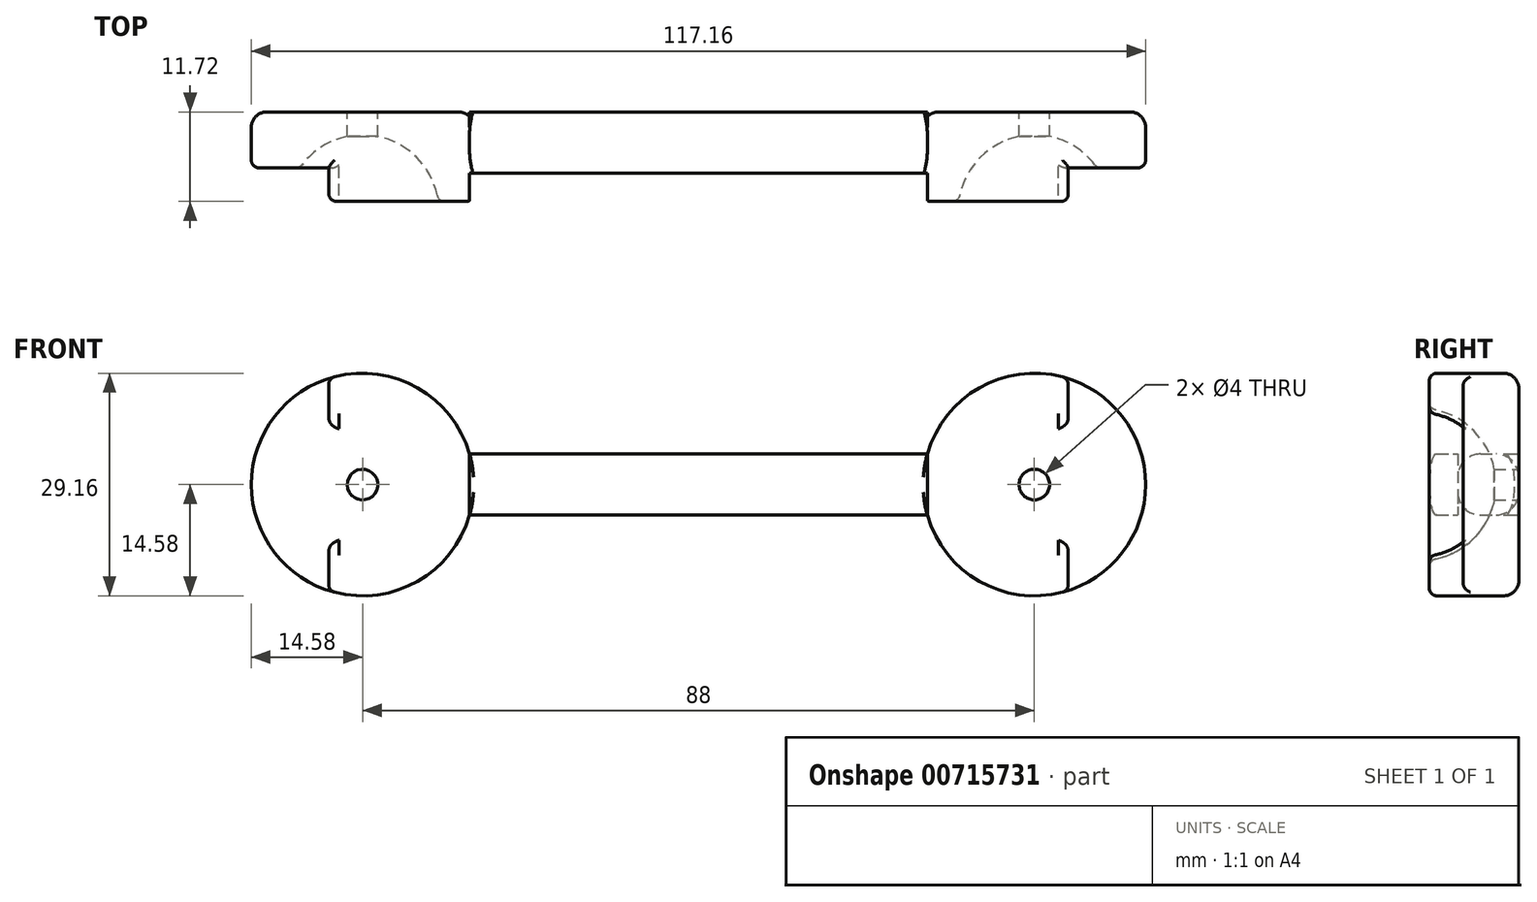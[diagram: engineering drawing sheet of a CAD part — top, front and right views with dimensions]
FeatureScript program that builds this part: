
annotation { "Feature Type Name" : "Feature", "Feature Type Description" : "" }
export const myFeature = defineFeature(function(context is Context, id is Id, definition is map)
    precondition{}
    {
        {
            var Q0;
            Q0=qCreatedBy(makeId("Front.planeOp"),FACE);
            var sketch = newSketch(context, id + "F0", { "sketchPlane" : qUnion([Q0])});
            skLineSegment(sketch, "E0.bottom", {"start": v(-30, 4) * mm, "end": v(30, 4) * mm});
            skLineSegment(sketch, "E0.top", {"start": v(-30, -4) * mm, "end": v(30, -4) * mm});
            skLineSegment(sketch, "E0.left", {"start": v(-30, 4) * mm, "end": v(-30, -4) * mm});
            skLineSegment(sketch, "E0.right", {"start": v(30, 4) * mm, "end": v(30, -4) * mm});
            skPoint(sketch, "E0.middle", {"position": v(0, 0) * mm});
            skCircle(sketch, "E1", {"center": v(-44, 0) * mm, "radius": 14.57 * mm});
            skCircle(sketch, "E2", {"center": v(44, 0) * mm, "radius": 14.57 * mm});
            skSolve(sketch);
        }
        {
            var Q0;
            {var subQ0=sQuery(id+"F0.wireOp",EDGE,"E1");var subQ1=sQuery(id+"F0.wireOp",EDGE,"E0.bottom");var subQ2=makeQuery(id+"F0.imprint","INTERSECT",VERTEX,{"derivedFrom":[subQ1,subQ0]});Q0=makeQuery(id+"F0.imprint","IMPRINT",FACE,{"disambiguationData":[TD([[makeQuery(id+"F0.imprint","IMPRINT",EDGE,{"disambiguationData":[TD([[subQ2,-1.0]])],"derivedFrom":subQ1}),-1.0]])]});}
            extrude(context, id + "F1", {"entities" : qUnion([Q0]), "depth" : 8 * mm, "offsetDistance" : 25 * mm});
        }
        {
            var Q0;
            {var subQ0=sQuery(id+"F0.wireOp",EDGE,"E0.left");Q0=makeQuery(id+"F0.imprint","IMPRINT",FACE,{"disambiguationData":[TD([[makeQuery(id+"F0.imprint","IMPRINT",EDGE,{"derivedFrom":subQ0}),-1.0]])]});}
            var Q1;
            Q1=makeQuery(id+"F0.imprint","IMPRINT",FACE,{"disambiguationData":[TD([[makeQuery(id+"F0.imprint","IMPRINT",EDGE,{"derivedFrom":sQuery(id+"F0.wireOp",EDGE,"DApRIKNj-3Abn-xKZV-fMbo-L7JkTV0Aw5cv")}),1.0]])]});
            var Q2;
            {var subQ0=sQuery(id+"F0.wireOp",EDGE,"E0.right");Q2=makeQuery(id+"F0.imprint","IMPRINT",FACE,{"disambiguationData":[TD([[makeQuery(id+"F0.imprint","IMPRINT",EDGE,{"derivedFrom":subQ0}),1.0]])]});}
            var Q3;
            Q3=makeQuery(id+"F0.imprint","IMPRINT",FACE,{"disambiguationData":[TD([[makeQuery(id+"F0.imprint","IMPRINT",EDGE,{"derivedFrom":sQuery(id+"F0.wireOp",EDGE,"rP7acSdx-QPYR-FfkY-qv1G-81ter26oukMQ")}),1.0]])]});
            extrude(context, id + "F2", {"entities" : qUnion([Q0, Q1, Q2, Q3]), "depth" : 13 * mm, "offsetDistance" : 25 * mm});
        }
        {
            var Q0;
            Q0=makeQuery(id+"F2.opExtrude","CAP_FACE",FACE,{"disambiguationData":[OSD([sQuery(id+"F0.wireOp",EDGE,"E0.bottom"),sQuery(id+"F0.wireOp",EDGE,"E0.top"),sQuery(id+"F0.wireOp",EDGE,"E0.left"),sQuery(id+"F0.wireOp",EDGE,"E1")])],"isStart":false});
            var sketch = newSketch(context, id + "F3", { "sketchPlane" : qUnion([Q0])});
            skCircle(sketch, "E3", {"center": v(-44, 0) * mm, "radius": 10 * mm});
            skSolve(sketch);
        }
        {
            var Q0;
            Q0=makeQuery(id+"F3.imprint","IMPRINT",FACE,{"disambiguationData":[TD([[makeQuery(id+"F3.imprint","IMPRINT",EDGE,{"derivedFrom":sQuery(id+"F3.wireOp",EDGE,"E3")}),1.0]])]});
            extrude(context, id + "F4", {"entities" : qUnion([Q0]), "operationType" : NewBodyOperationType.REMOVE, "oppositeDirection" : true, "depth" : 10 * mm, "offsetDistance" : 25 * mm});
        }
        {
            var Q0;
            Q0=makeQuery(id+"F4.boolean.opBoolean","COPY",FACE,{"derivedFrom":makeQuery(id+"F4.opExtrude","CAP_FACE",FACE,{"disambiguationData":[OSD([sQuery(id+"F3.wireOp",EDGE,"E3")])],"isStart":false})});
            fillet(context, id + "F5", {"entities" : qUnion([Q0]), "radius" : 10 * mm, "tangentPropagation" : true, "allowEdgeOverflow" : false});
        }
        {
            var Q0;
            Q0=makeQuery(id+"F2.opExtrude","CAP_FACE",FACE,{"disambiguationData":[OSD([sQuery(id+"F0.wireOp",EDGE,"E0.bottom"),sQuery(id+"F0.wireOp",EDGE,"E0.top"),sQuery(id+"F0.wireOp",EDGE,"E0.right"),sQuery(id+"F0.wireOp",EDGE,"E2")])],"isStart":false});
            var sketch = newSketch(context, id + "F6", { "sketchPlane" : qUnion([Q0])});
            skCircle(sketch, "E4", {"center": v(44, 0) * mm, "radius": 10 * mm});
            skSolve(sketch);
        }
        {
            var Q0;
            {var subQ0=sQuery(id+"F0.wireOp",EDGE,"E0.right");Q0=makeQuery(id+"F0.imprint","IMPRINT",FACE,{"disambiguationData":[TD([[makeQuery(id+"F0.imprint","IMPRINT",EDGE,{"derivedFrom":subQ0}),-1.0]])]});}
            extrude(context, id + "F7", {"entities" : qUnion([Q0]), "depth" : 8 * mm, "offsetDistance" : 25 * mm});
        }
        {
            var Q0;
            {var subQ0=sQuery(id+"F0.wireOp",EDGE,"E0.left");Q0=makeQuery(id+"F0.imprint","IMPRINT",FACE,{"disambiguationData":[TD([[makeQuery(id+"F0.imprint","IMPRINT",EDGE,{"derivedFrom":subQ0}),1.0]])]});}
            extrude(context, id + "F8", {"entities" : qUnion([Q0]), "depth" : 8 * mm, "offsetDistance" : 25 * mm});
        }
        {
            var Q0;
            Q0=makeQuery(id+"F6.imprint","IMPRINT",FACE,{"disambiguationData":[TD([[makeQuery(id+"F6.imprint","IMPRINT",EDGE,{"derivedFrom":sQuery(id+"F6.wireOp",EDGE,"E4")}),1.0]])]});
            extrude(context, id + "F9", {"entities" : qUnion([Q0]), "operationType" : NewBodyOperationType.REMOVE, "oppositeDirection" : true, "depth" : 10 * mm, "offsetDistance" : 25 * mm});
        }
        {
            var Q0;
            Q0=makeQuery(id+"F9.boolean.opBoolean","COPY",FACE,{"derivedFrom":makeQuery(id+"F9.opExtrude","CAP_FACE",FACE,{"disambiguationData":[OSD([sQuery(id+"F6.wireOp",EDGE,"E4")])],"isStart":false})});
            fillet(context, id + "F10", {"entities" : qUnion([Q0]), "radius" : 10 * mm, "tangentPropagation" : true, "allowEdgeOverflow" : false});
        }
        {
            var Q0;
            Q0=makeQuery(id+"F2.opExtrude","CAP_EDGE",EDGE,{"disambiguationData":[OSD([sQuery(id+"F0.wireOp",EDGE,"E2")])],"isStart":false});
            var Q1;
            Q1=makeQuery(id+"F2.opExtrude","CAP_EDGE",EDGE,{"disambiguationData":[OSD([sQuery(id+"F0.wireOp",EDGE,"E1")])],"isStart":false});
            fillet(context, id + "F11", {"entities" : qUnion([Q0, Q1]), "radius" : 1 * mm, "tangentPropagation" : true, "allowEdgeOverflow" : false});
        }
        {
            var Q0;
            Q0=makeQuery(id+"F5.opFillet","BLEND_EDGE",EDGE,{"blendedFrom":[makeQuery(id+"F4.boolean.opBoolean","COPY",EDGE,{"derivedFrom":makeQuery(id+"F4.opExtrude","CAP_EDGE",EDGE,{"disambiguationData":[OSD([sQuery(id+"F3.wireOp",EDGE,"E3")])],"isStart":false})}),makeQuery(id+"F2.opExtrude","CAP_FACE",FACE,{"disambiguationData":[OSD([sQuery(id+"F0.wireOp",EDGE,"E0.bottom"),sQuery(id+"F0.wireOp",EDGE,"E0.top"),sQuery(id+"F0.wireOp",EDGE,"E0.left"),sQuery(id+"F0.wireOp",EDGE,"E1")])],"isStart":false})],"blendedInto":[makeQuery(id+"F2.opExtrude","CAP_FACE",FACE,{"disambiguationData":[OSD([sQuery(id+"F0.wireOp",EDGE,"E0.bottom"),sQuery(id+"F0.wireOp",EDGE,"E0.top"),sQuery(id+"F0.wireOp",EDGE,"E0.left"),sQuery(id+"F0.wireOp",EDGE,"E1")])],"isStart":false})]});
            var Q1;
            Q1=makeQuery(id+"F10.opFillet","BLEND_EDGE",EDGE,{"blendedFrom":[makeQuery(id+"F9.boolean.opBoolean","COPY",EDGE,{"derivedFrom":makeQuery(id+"F9.opExtrude","CAP_EDGE",EDGE,{"disambiguationData":[OSD([sQuery(id+"F6.wireOp",EDGE,"E4")])],"isStart":false})}),makeQuery(id+"F2.opExtrude","CAP_FACE",FACE,{"disambiguationData":[OSD([sQuery(id+"F0.wireOp",EDGE,"E0.bottom"),sQuery(id+"F0.wireOp",EDGE,"E0.top"),sQuery(id+"F0.wireOp",EDGE,"E0.right"),sQuery(id+"F0.wireOp",EDGE,"E2")])],"isStart":false})],"blendedInto":[makeQuery(id+"F2.opExtrude","CAP_FACE",FACE,{"disambiguationData":[OSD([sQuery(id+"F0.wireOp",EDGE,"E0.bottom"),sQuery(id+"F0.wireOp",EDGE,"E0.top"),sQuery(id+"F0.wireOp",EDGE,"E0.right"),sQuery(id+"F0.wireOp",EDGE,"E2")])],"isStart":false})]});
            fillet(context, id + "F12", {"entities" : qUnion([Q0, Q1]), "radius" : 1 * mm, "tangentPropagation" : true, "allowEdgeOverflow" : false});
        }
        {
            var Q0;
            Q0=makeQuery(id+"F1.opExtrude","CAP_EDGE",EDGE,{"disambiguationData":[OSD([sQuery(id+"F0.wireOp",EDGE,"E0.bottom")])],"isStart":false});
            var Q1;
            Q1=makeQuery(id+"F1.opExtrude","CAP_EDGE",EDGE,{"disambiguationData":[OSD([sQuery(id+"F0.wireOp",EDGE,"E0.top")])],"isStart":false});
            var Q2;
            Q2=makeQuery(id+"F1.opExtrude","CAP_EDGE",EDGE,{"disambiguationData":[OSD([sQuery(id+"F0.wireOp",EDGE,"E0.top")])],"isStart":true});
            var Q3;
            Q3=makeQuery(id+"F1.opExtrude","CAP_EDGE",EDGE,{"disambiguationData":[OSD([sQuery(id+"F0.wireOp",EDGE,"E0.bottom")])],"isStart":true});
            fillet(context, id + "F13", {"entities" : qUnion([Q0, Q1, Q2, Q3]), "radius" : 3 * mm, "tangentPropagation" : true, "allowEdgeOverflow" : false});
        }
        {
            var Q0;
            Q0=makeQuery(id+"F2.opExtrude","CAP_EDGE",EDGE,{"disambiguationData":[OSD([sQuery(id+"F0.wireOp",EDGE,"E1")])],"isStart":true});
            var Q1;
            Q1=makeQuery(id+"F2.opExtrude","CAP_EDGE",EDGE,{"disambiguationData":[OSD([sQuery(id+"F0.wireOp",EDGE,"E2")])],"isStart":true});
            fillet(context, id + "F14", {"entities" : qUnion([Q0, Q1]), "radius" : 2 * mm, "tangentPropagation" : true, "allowEdgeOverflow" : false});
        }
        {
            var Q0;
            Q0=qCreatedBy(makeId("Front.planeOp"),FACE);
            var sketch = newSketch(context, id + "F15", { "sketchPlane" : qUnion([Q0])});
            skCircle(sketch, "E5", {"center": v(-44, 0) * mm, "radius": 2 * mm});
            skSolve(sketch);
        }
        {
            var Q0;
            Q0 = qSketchRegion(id + "F15", true);
            extrude(context, id + "F16", {"entities" : qUnion([Q0]), "operationType" : NewBodyOperationType.REMOVE, "endBound" : BoundingType.SYMMETRIC, "depth" : 25 * mm, "offsetDistance" : 25 * mm});
        }
        {
            var Q0;
            Q0=qCreatedBy(makeId("Front.planeOp"),FACE);
            var sketch = newSketch(context, id + "F17", { "sketchPlane" : qUnion([Q0])});
            skCircle(sketch, "E6", {"center": v(44, 0) * mm, "radius": 2 * mm});
            skSolve(sketch);
        }
        {
            var Q0;
            Q0 = qSketchRegion(id + "F17", true);
            extrude(context, id + "F18", {"entities" : qUnion([Q0]), "operationType" : NewBodyOperationType.REMOVE, "endBound" : BoundingType.SYMMETRIC, "depth" : 25 * mm, "offsetDistance" : 25 * mm});
        }
        {
            var Q0;
            Q0=makeQuery(id+"F2.opExtrude","SWEPT_BODY",BODY,{"disambiguationData":[OSD([sQuery(id+"F0.wireOp",EDGE,"E0.bottom"),sQuery(id+"F0.wireOp",EDGE,"E0.top"),sQuery(id+"F0.wireOp",EDGE,"E0.right"),sQuery(id+"F0.wireOp",EDGE,"E2")])]});
            var Q1;
            Q1=makeQuery(id+"F1.opExtrude","SWEPT_BODY",BODY,{"disambiguationData":[OSD([sQuery(id+"F0.wireOp",EDGE,"E0.bottom"),sQuery(id+"F0.wireOp",EDGE,"E0.top"),sQuery(id+"F0.wireOp",EDGE,"E1"),sQuery(id+"F0.wireOp",EDGE,"E2")])]});
            var Q2;
            Q2=makeQuery(id+"F8.opExtrude","SWEPT_BODY",BODY,{"disambiguationData":[OSD([sQuery(id+"F0.wireOp",EDGE,"E0.bottom"),sQuery(id+"F0.wireOp",EDGE,"E0.top"),sQuery(id+"F0.wireOp",EDGE,"E0.left"),sQuery(id+"F0.wireOp",EDGE,"E1")])]});
            var Q3;
            Q3=makeQuery(id+"F2.opExtrude","SWEPT_BODY",BODY,{"disambiguationData":[OSD([sQuery(id+"F0.wireOp",EDGE,"E0.bottom"),sQuery(id+"F0.wireOp",EDGE,"E0.top"),sQuery(id+"F0.wireOp",EDGE,"E0.left"),sQuery(id+"F0.wireOp",EDGE,"E1")])]});
            var Q4;
            Q4=makeQuery(id+"F7.opExtrude","SWEPT_BODY",BODY,{"disambiguationData":[OSD([sQuery(id+"F0.wireOp",EDGE,"E0.bottom"),sQuery(id+"F0.wireOp",EDGE,"E0.top"),sQuery(id+"F0.wireOp",EDGE,"E0.right"),sQuery(id+"F0.wireOp",EDGE,"E2")])]});
            booleanBodies(context, id + "F19", {"operationType" : BooleanOperationType.UNION, "tools" : qUnion([Q0, Q1, Q2, Q3, Q4])});
        }
        {
            var Q0;
            Q0=qCreatedBy(makeId("Right.planeOp"),FACE);
            var sketch = newSketch(context, id + "F20", { "sketchPlane" : qUnion([Q0])});
            skLineSegment(sketch, "E7", {"start": v(-11.72, 0) * mm, "end": v(-11.72, 17.2) * mm});
            skLineSegment(sketch, "E8", {"start": v(-11.72, 17.2) * mm, "end": v(-11.72, -18.6) * mm});
            skLineSegment(sketch, "E9", {"start": v(-11.72, -18.6) * mm, "end": v(-21.45, -18.6) * mm});
            skLineSegment(sketch, "E10", {"start": v(-21.45, -18.6) * mm, "end": v(-21.45, 17.2) * mm});
            skLineSegment(sketch, "E11", {"start": v(-21.45, 17.2) * mm, "end": v(-11.72, 17.2) * mm});
            skSolve(sketch);
        }
        {
            var Q0;
            Q0=qCreatedBy(makeId("Top.planeOp"),FACE);
            var sketch = newSketch(context, id + "F21", { "sketchPlane" : qUnion([Q0])});
            skLineSegment(sketch, "E12", {"start": v(48.44, -7.31) * mm, "end": v(48.44, -15.76) * mm});
            skLineSegment(sketch, "E13", {"start": v(48.44, -15.76) * mm, "end": v(59.98, -15.76) * mm});
            skLineSegment(sketch, "E14", {"start": v(48.44, -7.31) * mm, "end": v(59.98, -7.31) * mm});
            skLineSegment(sketch, "E15", {"start": v(59.98, -7.31) * mm, "end": v(59.98, -15.76) * mm});
            skLineSegment(sketch, "E16", {"start": v(58.58, -9.66) * mm, "end": v(59.98, -9.66) * mm});
            skLineSegment(sketch, "E17", {"start": v(-59.97, -7.31) * mm, "end": v(-59.97, -15.76) * mm});
            skLineSegment(sketch, "E18", {"start": v(-59.97, -15.76) * mm, "end": v(-48.42, -15.76) * mm});
            skLineSegment(sketch, "E19", {"start": v(-59.97, -7.31) * mm, "end": v(-48.42, -7.31) * mm});
            skLineSegment(sketch, "E20", {"start": v(-48.42, -7.31) * mm, "end": v(-48.42, -15.76) * mm});
            skLineSegment(sketch, "E21", {"start": v(52.83, -15.76) * mm, "end": v(52.83, -13) * mm});
            skSolve(sketch);
        }
        {
            var Q0;
            Q0 = qSketchRegion(id + "F21", true);
            extrude(context, id + "F22", {"entities" : qUnion([Q0]), "operationType" : NewBodyOperationType.REMOVE, "endBound" : BoundingType.SYMMETRIC, "depth" : 30 * mm, "offsetDistance" : 25 * mm});
        }
        {
            var Q0;
            Q0=makeQuery(id+"F21.imprint","IMPRINT",FACE,{"disambiguationData":[TD([[makeQuery(id+"F21.imprint","IMPRINT",EDGE,{"derivedFrom":sQuery(id+"F21.wireOp",EDGE,"E17")}),1.0]])]});
            extrude(context, id + "F23", {"entities" : qUnion([Q0]), "operationType" : NewBodyOperationType.REMOVE, "endBound" : BoundingType.SYMMETRIC, "oppositeDirection" : true, "depth" : 30 * mm, "offsetDistance" : 25 * mm});
        }
        {
            var Q0;
            Q0 = qSketchRegion(id + "F20", true);
            extrude(context, id + "F24", {"entities" : qUnion([Q0]), "operationType" : NewBodyOperationType.REMOVE, "endBound" : BoundingType.SYMMETRIC, "oppositeDirection" : true, "depth" : 150 * mm, "offsetDistance" : 25 * mm});
        }
        {
            var Q0;
            Q0=makeQuery(id+"F24.boolean.opBoolean","INTERSECT",EDGE,{"derivedFrom":[makeQuery(id+"F5.opFillet","BLEND_FACE",FACE,{"disambiguationData":[OSD([sQuery(id+"F3.wireOp",EDGE,"E3")])]}),makeQuery(id+"F24.opExtrude","SWEPT_FACE",FACE,{"disambiguationData":[OSD([sQuery(id+"F20.wireOp",EDGE,"E8")])]})]});
            var Q1;
            {var subQ0=sQuery(id+"F0.wireOp",EDGE,"E1");Q1=makeQuery(id+"F24.boolean.opBoolean","INTERSECT",EDGE,{"disambiguationData":[OD(1.0)],"derivedFrom":[makeQuery(id+"F19.opBoolean","MERGE",FACE,{"derivedFrom":[makeQuery(id+"F8.opExtrude","SWEPT_FACE",FACE,{"disambiguationData":[OSD([subQ0])]}),makeQuery(id+"F2.opExtrude","SWEPT_FACE",FACE,{"disambiguationData":[OSD([subQ0])]})]}),makeQuery(id+"F24.opExtrude","SWEPT_FACE",FACE,{"disambiguationData":[OSD([sQuery(id+"F20.wireOp",EDGE,"E8")])]})]});}
            var Q2;
            {var subQ0=sQuery(id+"F0.wireOp",EDGE,"E1");Q2=makeQuery(id+"F24.boolean.opBoolean","INTERSECT",EDGE,{"disambiguationData":[OD(0.0)],"derivedFrom":[makeQuery(id+"F19.opBoolean","MERGE",FACE,{"derivedFrom":[makeQuery(id+"F8.opExtrude","SWEPT_FACE",FACE,{"disambiguationData":[OSD([subQ0])]}),makeQuery(id+"F2.opExtrude","SWEPT_FACE",FACE,{"disambiguationData":[OSD([subQ0])]})]}),makeQuery(id+"F24.opExtrude","SWEPT_FACE",FACE,{"disambiguationData":[OSD([sQuery(id+"F20.wireOp",EDGE,"E8")])]})]});}
            var Q3;
            Q3=makeQuery(id+"F24.boolean.opBoolean","INTERSECT",EDGE,{"derivedFrom":[makeQuery(id+"F22.boolean.opBoolean","COPY",FACE,{"disambiguationData":[OD(0.0)],"derivedFrom":makeQuery(id+"F22.opExtrude","SWEPT_FACE",FACE,{"disambiguationData":[OSD([sQuery(id+"F21.wireOp",EDGE,"E20")])]})}),makeQuery(id+"F24.opExtrude","SWEPT_FACE",FACE,{"disambiguationData":[OSD([sQuery(id+"F20.wireOp",EDGE,"E8")])]})]});
            var Q4;
            Q4=makeQuery(id+"F24.boolean.opBoolean","INTERSECT",EDGE,{"derivedFrom":[makeQuery(id+"F22.boolean.opBoolean","COPY",FACE,{"disambiguationData":[OD(1.0)],"derivedFrom":makeQuery(id+"F22.opExtrude","SWEPT_FACE",FACE,{"disambiguationData":[OSD([sQuery(id+"F21.wireOp",EDGE,"E20")])]})}),makeQuery(id+"F24.opExtrude","SWEPT_FACE",FACE,{"disambiguationData":[OSD([sQuery(id+"F20.wireOp",EDGE,"E8")])]})]});
            var Q5;
            Q5=makeQuery(id+"F24.boolean.opBoolean","INTERSECT",EDGE,{"derivedFrom":[makeQuery(id+"F10.opFillet","BLEND_FACE",FACE,{"disambiguationData":[OSD([sQuery(id+"F6.wireOp",EDGE,"E4")])]}),makeQuery(id+"F24.opExtrude","SWEPT_FACE",FACE,{"disambiguationData":[OSD([sQuery(id+"F20.wireOp",EDGE,"E8")])]})]});
            var Q6;
            {var subQ0=sQuery(id+"F0.wireOp",EDGE,"E2");Q6=makeQuery(id+"F24.boolean.opBoolean","INTERSECT",EDGE,{"disambiguationData":[OD(0.0)],"derivedFrom":[makeQuery(id+"F19.opBoolean","MERGE",FACE,{"derivedFrom":[makeQuery(id+"F7.opExtrude","SWEPT_FACE",FACE,{"disambiguationData":[OSD([subQ0])]}),makeQuery(id+"F2.opExtrude","SWEPT_FACE",FACE,{"disambiguationData":[OSD([subQ0])]})]}),makeQuery(id+"F24.opExtrude","SWEPT_FACE",FACE,{"disambiguationData":[OSD([sQuery(id+"F20.wireOp",EDGE,"E8")])]})]});}
            var Q7;
            {var subQ0=sQuery(id+"F0.wireOp",EDGE,"E2");Q7=makeQuery(id+"F24.boolean.opBoolean","INTERSECT",EDGE,{"disambiguationData":[OD(1.0)],"derivedFrom":[makeQuery(id+"F19.opBoolean","MERGE",FACE,{"derivedFrom":[makeQuery(id+"F7.opExtrude","SWEPT_FACE",FACE,{"disambiguationData":[OSD([subQ0])]}),makeQuery(id+"F2.opExtrude","SWEPT_FACE",FACE,{"disambiguationData":[OSD([subQ0])]})]}),makeQuery(id+"F24.opExtrude","SWEPT_FACE",FACE,{"disambiguationData":[OSD([sQuery(id+"F20.wireOp",EDGE,"E8")])]})]});}
            var Q8;
            Q8=makeQuery(id+"F24.boolean.opBoolean","INTERSECT",EDGE,{"derivedFrom":[makeQuery(id+"F22.boolean.opBoolean","COPY",FACE,{"disambiguationData":[OD(0.0)],"derivedFrom":makeQuery(id+"F22.opExtrude","SWEPT_FACE",FACE,{"disambiguationData":[OSD([sQuery(id+"F21.wireOp",EDGE,"E12")])]})}),makeQuery(id+"F24.opExtrude","SWEPT_FACE",FACE,{"disambiguationData":[OSD([sQuery(id+"F20.wireOp",EDGE,"E8")])]})]});
            var Q9;
            Q9=makeQuery(id+"F24.boolean.opBoolean","INTERSECT",EDGE,{"derivedFrom":[makeQuery(id+"F22.boolean.opBoolean","COPY",FACE,{"disambiguationData":[OD(1.0)],"derivedFrom":makeQuery(id+"F22.opExtrude","SWEPT_FACE",FACE,{"disambiguationData":[OSD([sQuery(id+"F21.wireOp",EDGE,"E12")])]})}),makeQuery(id+"F24.opExtrude","SWEPT_FACE",FACE,{"disambiguationData":[OSD([sQuery(id+"F20.wireOp",EDGE,"E8")])]})]});
            var Q10;
            {var subQ0=sQuery(id+"F0.wireOp",EDGE,"E2");Q10=makeQuery(id+"F22.boolean.opBoolean","INTERSECT",EDGE,{"derivedFrom":[makeQuery(id+"F19.opBoolean","MERGE",FACE,{"derivedFrom":[makeQuery(id+"F7.opExtrude","SWEPT_FACE",FACE,{"disambiguationData":[OSD([subQ0])]}),makeQuery(id+"F2.opExtrude","SWEPT_FACE",FACE,{"disambiguationData":[OSD([subQ0])]})]}),makeQuery(id+"F22.opExtrude","SWEPT_FACE",FACE,{"disambiguationData":[OSD([sQuery(id+"F21.wireOp",EDGE,"E14")])]})]});}
            var Q11;
            Q11=makeQuery(id+"F22.boolean.opBoolean","INTERSECT",EDGE,{"derivedFrom":[makeQuery(id+"F10.opFillet","BLEND_FACE",FACE,{"disambiguationData":[OSD([sQuery(id+"F6.wireOp",EDGE,"E4")])]}),makeQuery(id+"F22.opExtrude","SWEPT_FACE",FACE,{"disambiguationData":[OSD([sQuery(id+"F21.wireOp",EDGE,"E14")])]})]});
            var Q12;
            Q12=makeQuery(id+"F22.boolean.opBoolean","INTERSECT",EDGE,{"derivedFrom":[makeQuery(id+"F5.opFillet","BLEND_FACE",FACE,{"disambiguationData":[OSD([sQuery(id+"F3.wireOp",EDGE,"E3")])]}),makeQuery(id+"F22.opExtrude","SWEPT_FACE",FACE,{"disambiguationData":[OSD([sQuery(id+"F21.wireOp",EDGE,"E19")])]})]});
            var Q13;
            {var subQ0=sQuery(id+"F0.wireOp",EDGE,"E1");Q13=makeQuery(id+"F22.boolean.opBoolean","INTERSECT",EDGE,{"derivedFrom":[makeQuery(id+"F19.opBoolean","MERGE",FACE,{"derivedFrom":[makeQuery(id+"F8.opExtrude","SWEPT_FACE",FACE,{"disambiguationData":[OSD([subQ0])]}),makeQuery(id+"F2.opExtrude","SWEPT_FACE",FACE,{"disambiguationData":[OSD([subQ0])]})]}),makeQuery(id+"F22.opExtrude","SWEPT_FACE",FACE,{"disambiguationData":[OSD([sQuery(id+"F21.wireOp",EDGE,"E19")])]})]});}
            var Q14;
            Q14=makeQuery(id+"F22.boolean.opBoolean","INTERSECT",EDGE,{"disambiguationData":[OD(1.0)],"derivedFrom":[makeQuery(id+"F5.opFillet","BLEND_FACE",FACE,{"disambiguationData":[OSD([sQuery(id+"F3.wireOp",EDGE,"E3")])]}),makeQuery(id+"F22.opExtrude","SWEPT_FACE",FACE,{"disambiguationData":[OSD([sQuery(id+"F21.wireOp",EDGE,"E20")])]})]});
            var Q15;
            {var subQ0=sQuery(id+"F0.wireOp",EDGE,"E1");Q15=makeQuery(id+"F22.boolean.opBoolean","INTERSECT",EDGE,{"disambiguationData":[OD(1.0)],"derivedFrom":[makeQuery(id+"F19.opBoolean","MERGE",FACE,{"derivedFrom":[makeQuery(id+"F8.opExtrude","SWEPT_FACE",FACE,{"disambiguationData":[OSD([subQ0])]}),makeQuery(id+"F2.opExtrude","SWEPT_FACE",FACE,{"disambiguationData":[OSD([subQ0])]})]}),makeQuery(id+"F22.opExtrude","SWEPT_FACE",FACE,{"disambiguationData":[OSD([sQuery(id+"F21.wireOp",EDGE,"E20")])]})]});}
            var Q16;
            {var subQ0=sQuery(id+"F0.wireOp",EDGE,"E1");Q16=makeQuery(id+"F22.boolean.opBoolean","INTERSECT",EDGE,{"disambiguationData":[OD(0.0)],"derivedFrom":[makeQuery(id+"F19.opBoolean","MERGE",FACE,{"derivedFrom":[makeQuery(id+"F8.opExtrude","SWEPT_FACE",FACE,{"disambiguationData":[OSD([subQ0])]}),makeQuery(id+"F2.opExtrude","SWEPT_FACE",FACE,{"disambiguationData":[OSD([subQ0])]})]}),makeQuery(id+"F22.opExtrude","SWEPT_FACE",FACE,{"disambiguationData":[OSD([sQuery(id+"F21.wireOp",EDGE,"E20")])]})]});}
            var Q17;
            Q17=makeQuery(id+"F22.boolean.opBoolean","INTERSECT",EDGE,{"disambiguationData":[OD(0.0)],"derivedFrom":[makeQuery(id+"F5.opFillet","BLEND_FACE",FACE,{"disambiguationData":[OSD([sQuery(id+"F3.wireOp",EDGE,"E3")])]}),makeQuery(id+"F22.opExtrude","SWEPT_FACE",FACE,{"disambiguationData":[OSD([sQuery(id+"F21.wireOp",EDGE,"E20")])]})]});
            var Q18;
            {var subQ0=sQuery(id+"F0.wireOp",EDGE,"E2");Q18=makeQuery(id+"F22.boolean.opBoolean","INTERSECT",EDGE,{"disambiguationData":[OD(0.0)],"derivedFrom":[makeQuery(id+"F19.opBoolean","MERGE",FACE,{"derivedFrom":[makeQuery(id+"F7.opExtrude","SWEPT_FACE",FACE,{"disambiguationData":[OSD([subQ0])]}),makeQuery(id+"F2.opExtrude","SWEPT_FACE",FACE,{"disambiguationData":[OSD([subQ0])]})]}),makeQuery(id+"F22.opExtrude","SWEPT_FACE",FACE,{"disambiguationData":[OSD([sQuery(id+"F21.wireOp",EDGE,"E12")])]})]});}
            var Q19;
            Q19=makeQuery(id+"F22.boolean.opBoolean","INTERSECT",EDGE,{"disambiguationData":[OD(0.0)],"derivedFrom":[makeQuery(id+"F10.opFillet","BLEND_FACE",FACE,{"disambiguationData":[OSD([sQuery(id+"F6.wireOp",EDGE,"E4")])]}),makeQuery(id+"F22.opExtrude","SWEPT_FACE",FACE,{"disambiguationData":[OSD([sQuery(id+"F21.wireOp",EDGE,"E12")])]})]});
            var Q20;
            Q20=makeQuery(id+"F22.boolean.opBoolean","INTERSECT",EDGE,{"disambiguationData":[OD(1.0)],"derivedFrom":[makeQuery(id+"F10.opFillet","BLEND_FACE",FACE,{"disambiguationData":[OSD([sQuery(id+"F6.wireOp",EDGE,"E4")])]}),makeQuery(id+"F22.opExtrude","SWEPT_FACE",FACE,{"disambiguationData":[OSD([sQuery(id+"F21.wireOp",EDGE,"E12")])]})]});
            var Q21;
            {var subQ0=sQuery(id+"F0.wireOp",EDGE,"E2");Q21=makeQuery(id+"F22.boolean.opBoolean","INTERSECT",EDGE,{"disambiguationData":[OD(1.0)],"derivedFrom":[makeQuery(id+"F19.opBoolean","MERGE",FACE,{"derivedFrom":[makeQuery(id+"F7.opExtrude","SWEPT_FACE",FACE,{"disambiguationData":[OSD([subQ0])]}),makeQuery(id+"F2.opExtrude","SWEPT_FACE",FACE,{"disambiguationData":[OSD([subQ0])]})]}),makeQuery(id+"F22.opExtrude","SWEPT_FACE",FACE,{"disambiguationData":[OSD([sQuery(id+"F21.wireOp",EDGE,"E12")])]})]});}
            fillet(context, id + "F25", {"entities" : qUnion([Q0, Q1, Q2, Q3, Q4, Q5, Q6, Q7, Q8, Q9, Q10, Q11, Q12, Q13, Q14, Q15, Q16, Q17, Q18, Q19, Q20, Q21]), "radius" : 1 * mm, "tangentPropagation" : true, "allowEdgeOverflow" : false});
        }
    });
